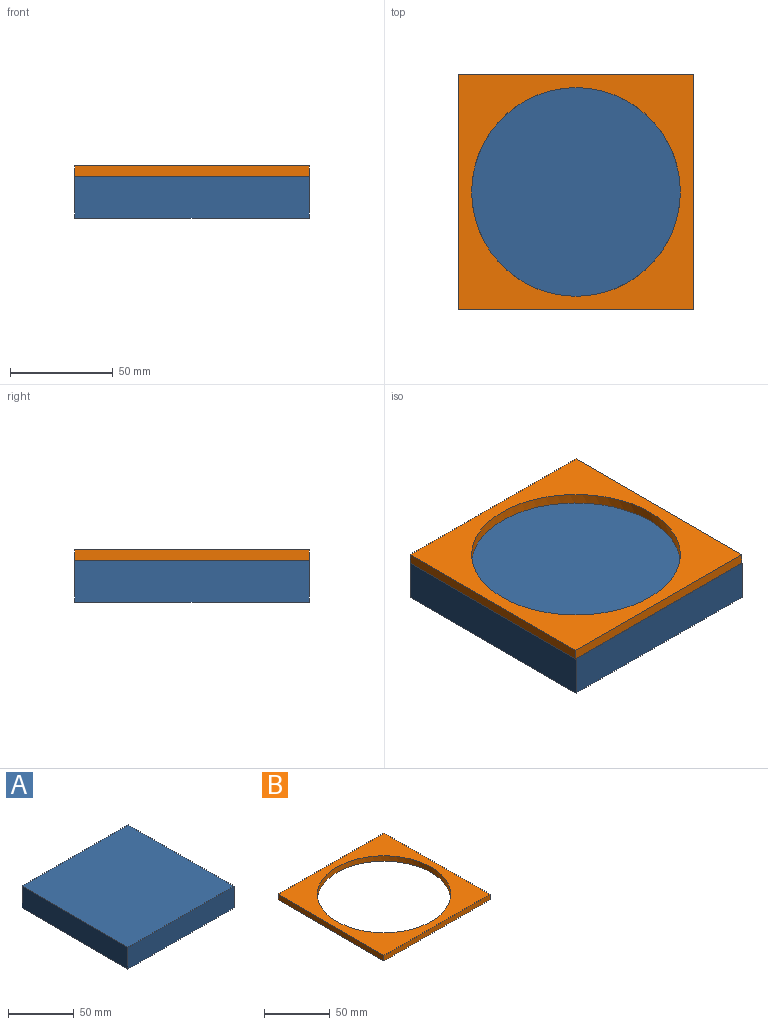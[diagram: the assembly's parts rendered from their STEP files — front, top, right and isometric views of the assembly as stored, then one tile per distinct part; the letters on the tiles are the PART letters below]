
ASSEMBLY  parts=2 mates=1
PART A: 6 faces, bbox 114.3x114.3x20.3 mm
  f0: plane 114.3x20.32mm, normal (0,-1,0), area 2322.6mm2, adj f1,f3,f4,f5
  f1: plane 114.3x20.32mm, normal (1,0,0), area 2322.6mm2, adj f0,f2,f4,f5
  f2: plane 114.3x20.32mm, normal (0,1,0), area 2322.6mm2, adj f1,f3,f4,f5
  f3: plane 114.3x20.32mm, normal (-1,0,0), area 2322.6mm2, adj f0,f2,f4,f5
  f4: plane 114.3x114.3mm, normal (0,0,1), area 13064.5mm2, adj f0,f1,f2,f3
  f5: plane 114.3x114.3mm, normal (0,0,-1), area 13064.5mm2, adj f0,f1,f2,f3
PART B: 7 faces, bbox 114.3x114.3x5.1 mm
  f0: plane 114.3x5.08mm, normal (1,0,0), area 580.6mm2, adj f1,f3,f4,f5
  f1: plane 114.3x5.08mm, normal (0,1,0), area 580.6mm2, adj f0,f2,f4,f5
  f2: plane 114.3x5.08mm, normal (-1,0,0), area 580.6mm2, adj f1,f3,f4,f5
  f3: plane 114.3x5.08mm, normal (0,-1,0), area 580.6mm2, adj f0,f2,f4,f5
  f4: plane 114.3x114.3mm, normal (0,0,1), area 4957.2mm2, adj f0,f1,f2,f3,f6
  f5: plane 114.3x114.3mm, normal (0,0,-1), area 4957.2mm2, adj f0,f1,f2,f3,f6
  f6: cylinder r=50.8mm len=101.6mm, axis (0,0,-1), area 1621.5mm2, adj f4,f5
PLACE A t=(-12.5,-7.21,-10.15)mm fixed
PLACE B t=(-12.5,-7.21,10.17)mm
MATE fastened A.f4 <-> B.f5  axis (0,0,1) through (44.65,49.94,10.17)mm
